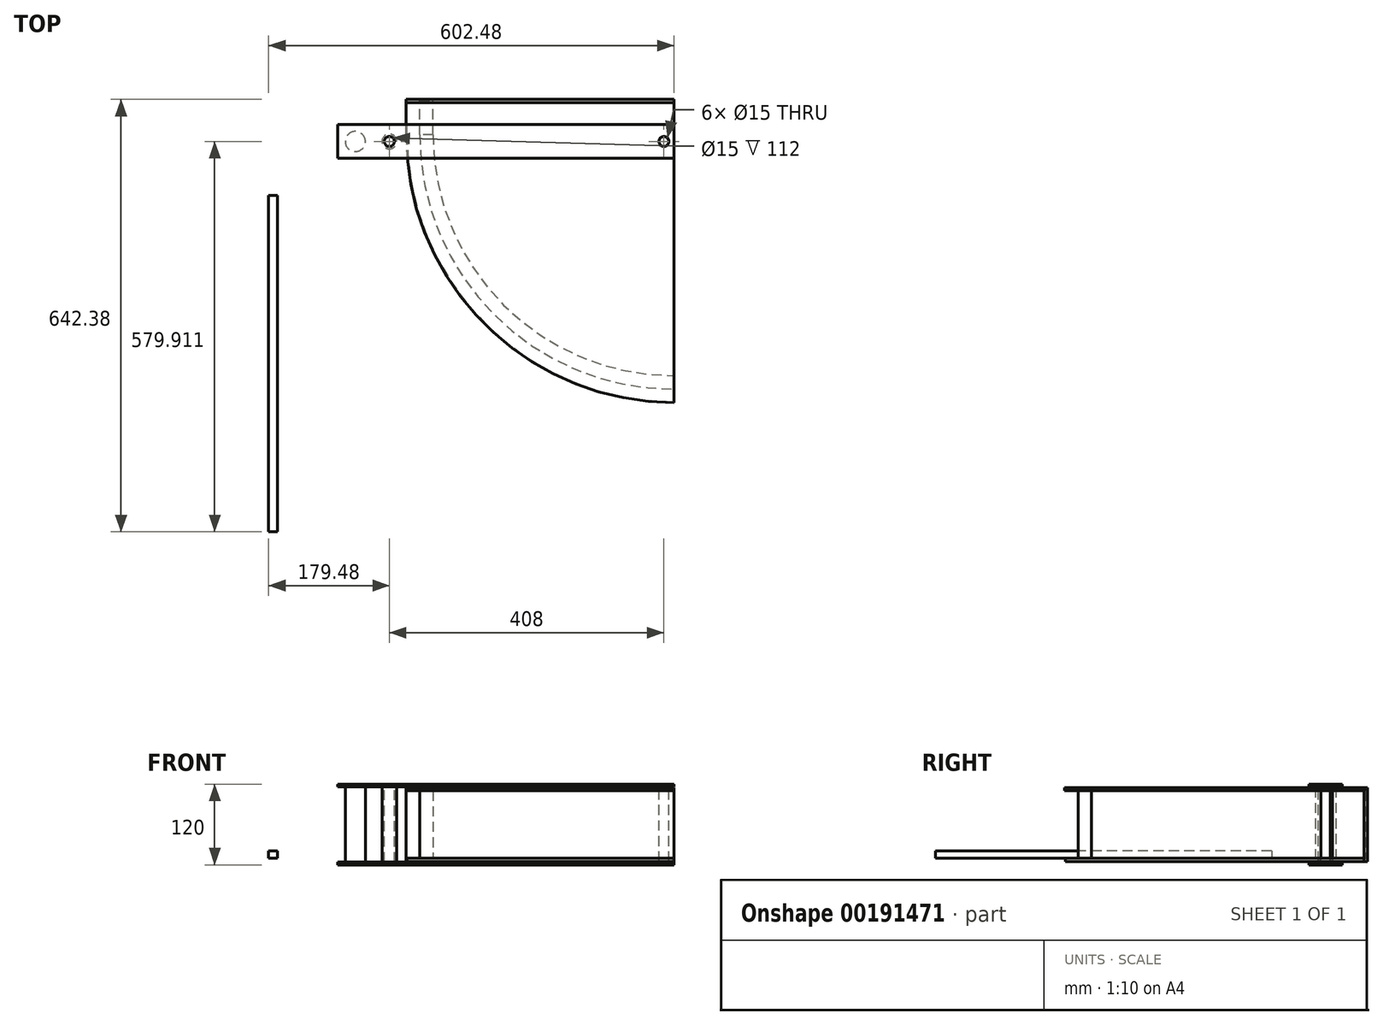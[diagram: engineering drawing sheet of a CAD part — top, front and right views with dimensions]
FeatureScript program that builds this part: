
annotation { "Feature Type Name" : "Feature", "Feature Type Description" : "" }
export const myFeature = defineFeature(function(context is Context, id is Id, definition is map)
    precondition{}
    {
        {
            var Q0;
            Q0=qCreatedBy(makeId("Top.planeOp"),FACE);
            var sketch = newSketch(context, id + "F0", { "sketchPlane" : qUnion([Q0])});
            skLineSegment(sketch, "E0", {"start": v(0, 0) * mm, "end": v(-378, 0) * mm});
            skArc(sketch, "E1", {"start": v(-378, 0) * mm, "mid": v(-267.29, -267.29) * mm, "end": v(0, -378) * mm});
            skLineSegment(sketch, "E2", {"start": v(0, 0) * mm, "end": v(0, -378) * mm});
            skArc(sketch, "E3.0", {"start": v(-358, 0) * mm, "mid": v(-253.14, -253.14) * mm, "end": v(0, -358) * mm});
            skLineSegment(sketch, "E4.top", {"start": v(-378, 50) * mm, "end": v(-358, 50) * mm});
            skLineSegment(sketch, "E4.left", {"start": v(-378, 0) * mm, "end": v(-378, 50) * mm});
            skLineSegment(sketch, "E4.right", {"start": v(-358, 0) * mm, "end": v(-358, 50) * mm});
            skSolve(sketch);
        }
        {
            var Q0;
            {var subQ0=sQuery(id+"F0.wireOp",EDGE,"E1");Q0=makeQuery(id+"F0.imprint","IMPRINT",FACE,{"disambiguationData":[TD([[makeQuery(id+"F0.imprint","IMPRINT",EDGE,{"derivedFrom":subQ0}),1.0]])]});}
            var Q1;
            Q1=makeQuery(id+"F0.imprint","IMPRINT",FACE,{"disambiguationData":[TD([[makeQuery(id+"F0.imprint","IMPRINT",EDGE,{"derivedFrom":sQuery(id+"F0.wireOp",EDGE,"E4.bottom")}),1.0]])]});
            extrude(context, id + "F1", {"entities" : qUnion([Q0, Q1]), "depth" : 100 * mm});
        }
        {
            var Q0;
            Q0=makeQuery(id+"F1.opExtrude","CAP_FACE",FACE,{"disambiguationData":[OSD([sQuery(id+"F0.wireOp",EDGE,"E0"),sQuery(id+"F0.wireOp",EDGE,"E1"),sQuery(id+"F0.wireOp",EDGE,"E2"),sQuery(id+"F0.wireOp",EDGE,"E3.0")])],"isStart":true});
            cPlane(context, id + "F2", {"entities" : qUnion([Q0]), "cplaneType" : CPlaneType.OFFSET, "offset" : 0 * mm, "width" : 150 * mm, "height" : 150 * mm});
        }
        {
            var Q0;
            Q0=qCreatedBy(id+"F2.planeOp",FACE);
            var sketch = newSketch(context, id + "F3", { "sketchPlane" : qUnion([Q0])});
            skLineSegment(sketch, "E5", {"start": v(0, 0) * mm, "end": v(0, 396.9) * mm});
            skLineSegment(sketch, "E6", {"start": v(0, 0) * mm, "end": v(-396.9, 0) * mm});
            skArc(sketch, "E7", {"start": v(0, 378) * mm, "mid": v(-267.29, 267.29) * mm, "end": v(-378, 0) * mm});
            skArc(sketch, "E8.0", {"start": v(0, 396.9) * mm, "mid": v(-280.65, 280.65) * mm, "end": v(-396.9, 0) * mm});
            skLineSegment(sketch, "E9.bottom", {"start": v(-396.9, 0) * mm, "end": v(0, 0) * mm});
            skLineSegment(sketch, "E9.top", {"start": v(-396.9, -47.25) * mm, "end": v(0, -47.25) * mm});
            skLineSegment(sketch, "E9.left", {"start": v(-396.9, 0) * mm, "end": v(-396.9, -47.25) * mm});
            skLineSegment(sketch, "E9.right", {"start": v(0, 0) * mm, "end": v(0, -47.25) * mm});
            skSolve(sketch);
        }
        {
            var Q0;
            Q0=qSketchRegion(id+"F3",true);
            extrude(context, id + "F4", {"entities" : qUnion([Q0]), "depth" : 5 * mm});
        }
        {
            var Q0;
            Q0=makeQuery(id+"F1.opExtrude","CAP_FACE",FACE,{"disambiguationData":[OSD([sQuery(id+"F0.wireOp",EDGE,"E0"),sQuery(id+"F0.wireOp",EDGE,"E1"),sQuery(id+"F0.wireOp",EDGE,"E2"),sQuery(id+"F0.wireOp",EDGE,"E3.0")])],"isStart":false});
            cPlane(context, id + "F5", {"entities" : qUnion([Q0]), "cplaneType" : CPlaneType.OFFSET, "offset" : 0 * mm, "width" : 150 * mm, "height" : 150 * mm});
        }
        {
            var Q0;
            Q0=qCreatedBy(id+"F5.planeOp",FACE);
            var sketch = newSketch(context, id + "F6", { "sketchPlane" : qUnion([Q0])});
            skLineSegment(sketch, "E10", {"start": v(0, 0) * mm, "end": v(0, -398) * mm});
            skLineSegment(sketch, "E11", {"start": v(0, 0) * mm, "end": v(-398, 0) * mm});
            skArc(sketch, "E12.0", {"start": v(-398, 0) * mm, "mid": v(-281.43, -281.43) * mm, "end": v(0, -398) * mm});
            skLineSegment(sketch, "E13.bottom", {"start": v(-398, 0) * mm, "end": v(0, 0) * mm});
            skLineSegment(sketch, "E13.top", {"start": v(-398, 47.38) * mm, "end": v(0, 47.38) * mm});
            skLineSegment(sketch, "E13.left", {"start": v(-398, 0) * mm, "end": v(-398, 47.38) * mm});
            skLineSegment(sketch, "E13.right", {"start": v(0, 0) * mm, "end": v(0, 47.38) * mm});
            skSolve(sketch);
        }
        {
            var Q0;
            Q0=qSketchRegion(id+"F6",true);
            extrude(context, id + "F7", {"entities" : qUnion([Q0]), "depth" : 5 * mm});
        }
        {
            var Q0;
            Q0=makeQuery(id+"F4.opExtrude","SWEPT_FACE",FACE,{"disambiguationData":[OSD([sQuery(id+"F3.wireOp",EDGE,"E9.top")])]});
            cPlane(context, id + "F8", {"entities" : qUnion([Q0]), "cplaneType" : CPlaneType.OFFSET, "offset" : 0 * mm, "width" : 150 * mm, "height" : 150 * mm});
        }
        {
            var Q0;
            Q0=qCreatedBy(id+"F8.planeOp",FACE);
            var sketch = newSketch(context, id + "F9", { "sketchPlane" : qUnion([Q0])});
            skLineSegment(sketch, "E14", {"start": v(0, -5) * mm, "end": v(0, 105) * mm});
            skLineSegment(sketch, "E15", {"start": v(0, -5) * mm, "end": v(398, -5) * mm});
            skLineSegment(sketch, "E16", {"start": v(398, -5) * mm, "end": v(398, 105) * mm});
            skLineSegment(sketch, "E17", {"start": v(398, 105) * mm, "end": v(0, 105) * mm});
            skSolve(sketch);
        }
        {
            var Q0;
            Q0=qSketchRegion(id+"F9",true);
            extrude(context, id + "F10", {"entities" : qUnion([Q0]), "depth" : 5.1 * mm});
        }
        {
            var Q0;
            Q0=makeQuery(id+"F7.opExtrude","CAP_FACE",FACE,{"disambiguationData":[OSD([sQuery(id+"F6.wireOp",EDGE,"E10"),sQuery(id+"F6.wireOp",EDGE,"E12.0"),sQuery(id+"F6.wireOp",EDGE,"E13.top"),sQuery(id+"F6.wireOp",EDGE,"E13.left"),sQuery(id+"F6.wireOp",EDGE,"E13.right")])],"isStart":false});
            var sketch = newSketch(context, id + "F11", { "sketchPlane" : qUnion([Q0])});
            skCircle(sketch, "E18", {"center": v(-15, -10.12) * mm, "radius": 7.5 * mm});
            skSolve(sketch);
        }
        {
            var Q0;
            Q0=qSketchRegion(id+"F11",true);
            extrude(context, id + "F12", {"entities" : qUnion([Q0]), "operationType" : NewBodyOperationType.REMOVE, "endBound" : BoundingType.THROUGH_ALL, "oppositeDirection" : true, "depth" : 42 * mm});
        }
        {
            var Q0;
            Q0=makeQuery(id+"F7.opExtrude","CAP_FACE",FACE,{"disambiguationData":[OSD([sQuery(id+"F6.wireOp",EDGE,"E10"),sQuery(id+"F6.wireOp",EDGE,"E12.0"),sQuery(id+"F6.wireOp",EDGE,"E13.top"),sQuery(id+"F6.wireOp",EDGE,"E13.left"),sQuery(id+"F6.wireOp",EDGE,"E13.right")])],"isStart":false});
            cPlane(context, id + "F13", {"entities" : qUnion([Q0]), "cplaneType" : CPlaneType.OFFSET, "offset" : 5 * mm, "width" : 150 * mm, "height" : 150 * mm});
        }
        {
            var Q0;
            Q0=qCreatedBy(id+"F13.planeOp",FACE);
            var sketch = newSketch(context, id + "F14", { "sketchPlane" : qUnion([Q0])});
            skCircle(sketch, "E19", {"center": v(-15, -10.12) * mm, "radius": 7.25 * mm});
            skSolve(sketch);
        }
        {
            var Q0;
            Q0=qSketchRegion(id+"F14",true);
            extrude(context, id + "F15", {"entities" : qUnion([Q0]), "oppositeDirection" : true, "depth" : 120 * mm});
        }
        {
            var Q0;
            Q0=makeQuery(id+"F15.opExtrude","CAP_FACE",FACE,{"disambiguationData":[OSD([sQuery(id+"F14.wireOp",EDGE,"E19")])],"isStart":true});
            cPlane(context, id + "F16", {"entities" : qUnion([Q0]), "cplaneType" : CPlaneType.OFFSET, "offset" : 0 * mm, "width" : 150 * mm, "height" : 150 * mm});
        }
        {
            var Q0;
            Q0=qCreatedBy(id+"F16.planeOp",FACE);
            var sketch = newSketch(context, id + "F17", { "sketchPlane" : qUnion([Q0])});
            skLineSegment(sketch, "E20.bottom", {"start": v(0, -35.12) * mm, "end": v(-500, -35.12) * mm});
            skLineSegment(sketch, "E20.top", {"start": v(0, 14.88) * mm, "end": v(-500, 14.88) * mm});
            skLineSegment(sketch, "E20.left", {"start": v(0, -35.12) * mm, "end": v(0, 14.88) * mm});
            skLineSegment(sketch, "E20.right", {"start": v(-500, -35.12) * mm, "end": v(-500, 14.88) * mm});
            skCircle(sketch, "E21", {"center": v(-15, -10.12) * mm, "radius": 7.5 * mm});
            skCircle(sketch, "E22", {"center": v(-423, -10.12) * mm, "radius": 7.5 * mm});
            skSolve(sketch);
        }
        {
            var Q0;
            Q0=qSketchRegion(id+"F17",true);
            extrude(context, id + "F18", {"entities" : qUnion([Q0]), "operationType" : NewBodyOperationType.ADD, "oppositeDirection" : true, "depth" : 4 * mm});
        }
        {
            var Q0;
            Q0=qCreatedBy(id+"F5.planeOp",FACE);
            cPlane(context, id + "F19", {"entities" : qUnion([Q0]), "cplaneType" : CPlaneType.OFFSET, "offset" : 50 * mm, "oppositeDirection" : true, "width" : 150 * mm, "height" : 150 * mm});
        }
        {
            var Q0;
            Q0=makeQuery(id+"F18.opExtrude","SWEPT_BODY",BODY,{"disambiguationData":[OSD([sQuery(id+"F17.wireOp",EDGE,"E20.bottom"),sQuery(id+"F17.wireOp",EDGE,"E20.top"),sQuery(id+"F17.wireOp",EDGE,"E20.left"),sQuery(id+"F17.wireOp",EDGE,"E20.right"),sQuery(id+"F17.wireOp",EDGE,"E21")])]});
            var Q1;
            Q1=qCreatedBy(id+"F19.planeOp",FACE);
            mirror(context, id + "F20", {"entities" : qUnion([Q0]), "mirrorPlane" : qUnion([Q1])});
        }
        {
            var Q0;
            Q0=makeQuery(id+"F0.imprint","IMPRINT",FACE,{"disambiguationData":[TD([[makeQuery(id+"F0.imprint","IMPRINT",EDGE,{"derivedFrom":sQuery(id+"F0.wireOp",EDGE,"E4.top")}),-1.0]])]});
            extrude(context, id + "F21", {"entities" : qUnion([Q0]), "depth" : 100 * mm});
        }
        {
            var Q0;
            Q0=makeQuery(id+"F20.opPattern","COPY",FACE,{"derivedFrom":makeQuery(id+"F18.opExtrude","CAP_FACE",FACE,{"disambiguationData":[OSD([sQuery(id+"F17.wireOp",EDGE,"E20.bottom"),sQuery(id+"F17.wireOp",EDGE,"E20.top"),sQuery(id+"F17.wireOp",EDGE,"E20.left"),sQuery(id+"F17.wireOp",EDGE,"E20.right"),sQuery(id+"F17.wireOp",EDGE,"E21"),sQuery(id+"F17.wireOp",EDGE,"E22")])],"isStart":false}),"instanceName":"1"});
            var sketch = newSketch(context, id + "F22", { "sketchPlane" : qUnion([Q0])});
            skCircle(sketch, "E23", {"center": v(-473.58, -10.12) * mm, "radius": 15 * mm});
            skPoint(sketch, "E23.centerSnap0", {"position": v(-500, -10.12) * mm});
            skSolve(sketch);
        }
        {
            var Q0;
            Q0 = qSketchRegion(id + "F22", true);
            extrude(context, id + "F23", {"entities" : qUnion([Q0]), "endBound" : BoundingType.UP_TO_NEXT, "depth" : 25 * mm});
        }
        {
            var Q0;
            Q0=makeQuery(id+"F18.opExtrude","CAP_FACE",FACE,{"disambiguationData":[OSD([sQuery(id+"F17.wireOp",EDGE,"E20.bottom"),sQuery(id+"F17.wireOp",EDGE,"E20.top"),sQuery(id+"F17.wireOp",EDGE,"E20.left"),sQuery(id+"F17.wireOp",EDGE,"E20.right"),sQuery(id+"F17.wireOp",EDGE,"E21"),sQuery(id+"F17.wireOp",EDGE,"E22")])],"isStart":false});
            var sketch = newSketch(context, id + "F24", { "sketchPlane" : qUnion([Q0])});
            skCircle(sketch, "E24", {"center": v(-423, 10.12) * mm, "radius": 7.5 * mm});
            skCircle(sketch, "E25", {"center": v(-423, 10.12) * mm, "radius": 11 * mm});
            skSolve(sketch);
        }
        {
            var Q0;
            Q0 = qSketchRegion(id + "F24", true);
            extrude(context, id + "F25", {"entities" : qUnion([Q0]), "endBound" : BoundingType.UP_TO_NEXT, "depth" : 25 * mm});
        }
        {
            var Q0;
            Q0=qCreatedBy(makeId("Top.planeOp"),FACE);
            var sketch = newSketch(context, id + "F26", { "sketchPlane" : qUnion([Q0])});
            skLineSegment(sketch, "E26.bottom", {"start": v(-602.48, -90.03) * mm, "end": v(-589.48, -90.03) * mm});
            skLineSegment(sketch, "E26.top", {"start": v(-602.48, -590.03) * mm, "end": v(-589.48, -590.03) * mm});
            skLineSegment(sketch, "E26.left", {"start": v(-602.48, -90.03) * mm, "end": v(-602.48, -590.03) * mm});
            skLineSegment(sketch, "E26.right", {"start": v(-589.48, -90.03) * mm, "end": v(-589.48, -590.03) * mm});
            skSolve(sketch);
        }
        {
            var Q0;
            Q0 = qSketchRegion(id + "F26", true);
            extrude(context, id + "F27", {"entities" : qUnion([Q0]), "depth" : 11 * mm});
        }
    });
